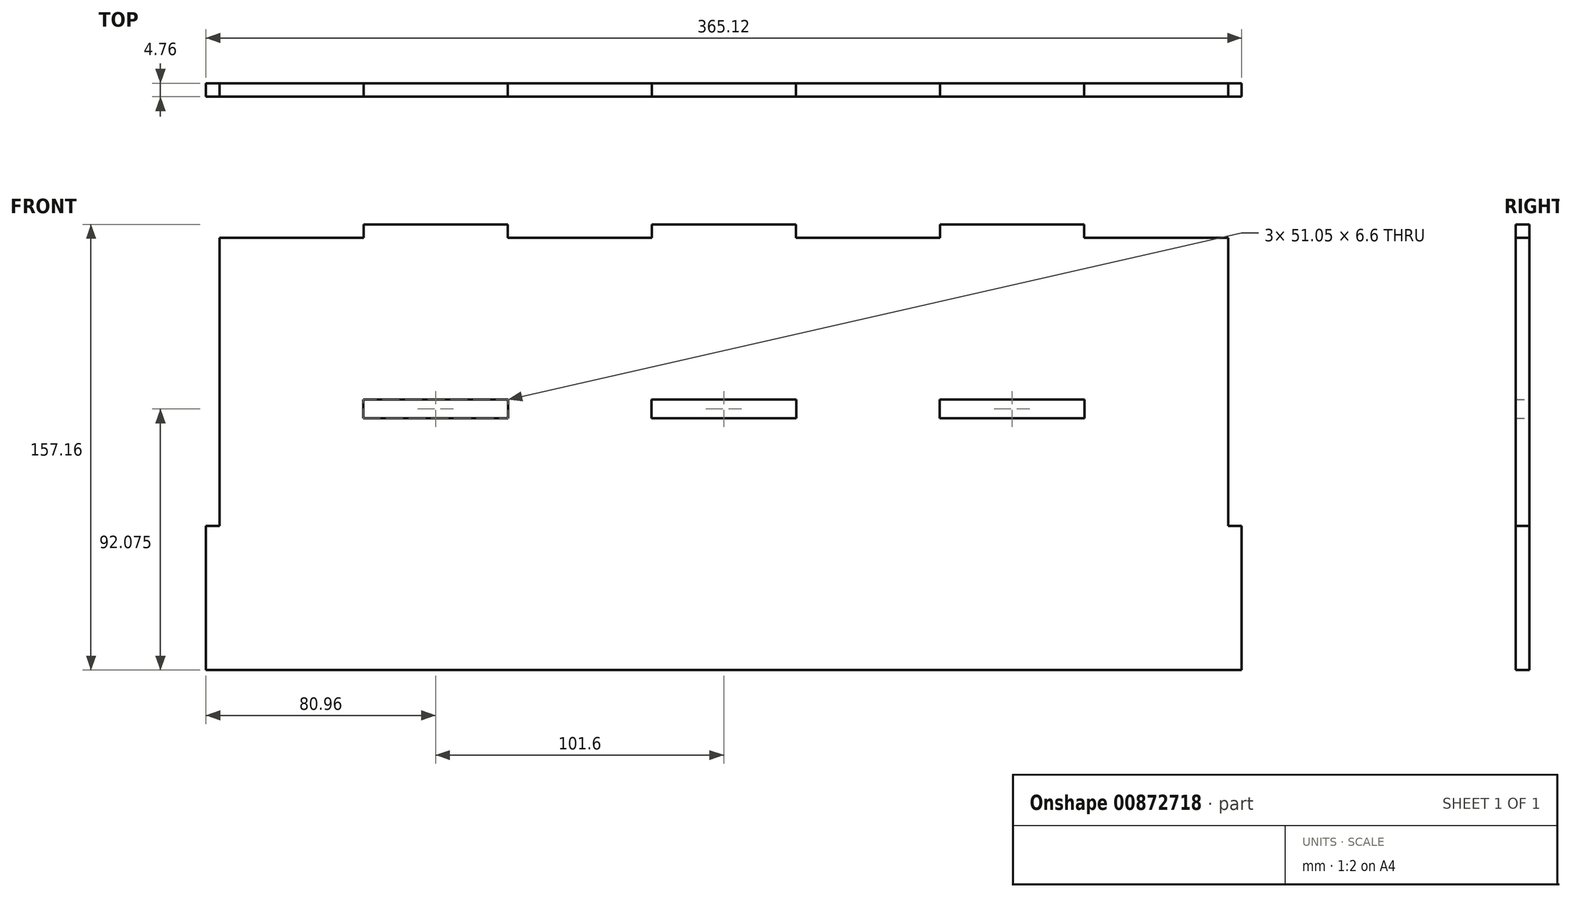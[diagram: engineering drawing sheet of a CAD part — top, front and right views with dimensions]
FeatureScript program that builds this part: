
annotation { "Feature Type Name" : "Feature", "Feature Type Description" : "" }
export const myFeature = defineFeature(function(context is Context, id is Id, definition is map)
    precondition{}
    {
        {
            var Q0;
            Q0=qCreatedBy(makeId("Front.planeOp"),FACE);
            var sketch = newSketch(context, id + "F0", { "sketchPlane" : qUnion([Q0])});
            skLineSegment(sketch, "E0.bottom", {"start": v(-182.56, 76.2) * mm, "end": v(182.56, 76.2) * mm});
            skLineSegment(sketch, "E0.top", {"start": v(-182.56, -76.2) * mm, "end": v(182.56, -76.2) * mm});
            skLineSegment(sketch, "E0.left", {"start": v(-182.56, 76.2) * mm, "end": v(-182.56, -76.2) * mm});
            skLineSegment(sketch, "E0.right", {"start": v(182.56, 76.2) * mm, "end": v(182.56, -76.2) * mm});
            skPoint(sketch, "E0.middle", {"position": v(0, 0) * mm});
            skLineSegment(sketch, "E1.0", {"start": v(-177.8, 76.2) * mm, "end": v(-177.8, -76.2) * mm});
            skLineSegment(sketch, "E2.0", {"start": v(177.8, 76.2) * mm, "end": v(177.8, -76.2) * mm});
            skLineSegment(sketch, "E3.bottom", {"start": v(-127, 19.05) * mm, "end": v(-76.2, 19.05) * mm});
            skLineSegment(sketch, "E3.top", {"start": v(-127, 12.7) * mm, "end": v(-76.2, 12.7) * mm});
            skLineSegment(sketch, "E3.left", {"start": v(-127, 19.05) * mm, "end": v(-127, 12.7) * mm});
            skLineSegment(sketch, "E3.right", {"start": v(-76.2, 19.05) * mm, "end": v(-76.2, 12.7) * mm});
            skLineSegment(sketch, "E4.0", {"start": v(-127.13, 19.18) * mm, "end": v(-76.07, 19.18) * mm});
            skLineSegment(sketch, "E4.1", {"start": v(-127.13, 19.18) * mm, "end": v(-127.13, 12.57) * mm});
            skLineSegment(sketch, "E4.2", {"start": v(-127.13, 12.57) * mm, "end": v(-76.07, 12.57) * mm});
            skLineSegment(sketch, "E4.3", {"start": v(-76.07, 19.18) * mm, "end": v(-76.07, 12.57) * mm});
            skLineSegment(sketch, "E5.1.0.0", {"start": v(-25.53, 19.18) * mm, "end": v(-25.53, 12.57) * mm});
            skLineSegment(sketch, "E5.1.0.1", {"start": v(-25.53, 19.18) * mm, "end": v(25.53, 19.18) * mm});
            skLineSegment(sketch, "E5.1.0.2", {"start": v(-25.53, 12.57) * mm, "end": v(25.53, 12.57) * mm});
            skLineSegment(sketch, "E5.1.0.3", {"start": v(25.4, 19.05) * mm, "end": v(25.4, 12.7) * mm});
            skLineSegment(sketch, "E5.1.0.4", {"start": v(-25.4, 19.05) * mm, "end": v(25.4, 19.05) * mm});
            skLineSegment(sketch, "E5.1.0.5", {"start": v(25.53, 19.18) * mm, "end": v(25.53, 12.57) * mm});
            skLineSegment(sketch, "E5.1.0.6", {"start": v(-25.4, 19.05) * mm, "end": v(-25.4, 12.7) * mm});
            skLineSegment(sketch, "E5.1.0.7", {"start": v(-25.4, 12.7) * mm, "end": v(25.4, 12.7) * mm});
            skLineSegment(sketch, "E5.2.0.0", {"start": v(76.07, 19.18) * mm, "end": v(76.07, 12.57) * mm});
            skLineSegment(sketch, "E5.2.0.1", {"start": v(76.07, 19.18) * mm, "end": v(127.13, 19.18) * mm});
            skLineSegment(sketch, "E5.2.0.2", {"start": v(76.07, 12.57) * mm, "end": v(127.13, 12.57) * mm});
            skLineSegment(sketch, "E5.2.0.3", {"start": v(127, 19.05) * mm, "end": v(127, 12.7) * mm});
            skLineSegment(sketch, "E5.2.0.4", {"start": v(76.2, 19.05) * mm, "end": v(127, 19.05) * mm});
            skLineSegment(sketch, "E5.2.0.5", {"start": v(127.13, 19.18) * mm, "end": v(127.13, 12.57) * mm});
            skLineSegment(sketch, "E5.2.0.6", {"start": v(76.2, 19.05) * mm, "end": v(76.2, 12.7) * mm});
            skLineSegment(sketch, "E5.2.0.7", {"start": v(76.2, 12.7) * mm, "end": v(127, 12.7) * mm});
            skLineSegment(sketch, "E5.direction1", {"start": v(-127, 12.7) * mm, "end": v(-25.4, 12.7) * mm, "construction": true});
            skLineSegment(sketch, "E6.bottom", {"start": v(-182.56, -76.2) * mm, "end": v(-177.8, -76.2) * mm});
            skLineSegment(sketch, "E6.top", {"start": v(-182.56, -25.4) * mm, "end": v(-177.8, -25.4) * mm});
            skLineSegment(sketch, "E6.left", {"start": v(-182.56, -76.2) * mm, "end": v(-182.56, -25.4) * mm});
            skLineSegment(sketch, "E6.right", {"start": v(-177.8, -76.2) * mm, "end": v(-177.8, -25.4) * mm});
            skLineSegment(sketch, "E7", {"start": v(0, 76.2) * mm, "end": v(0, -76.2) * mm, "construction": true});
            skLineSegment(sketch, "E8.MirrorCS", {"start": v(182.56, -76.2) * mm, "end": v(177.8, -76.2) * mm});
            skLineSegment(sketch, "E9.MirrorCS", {"start": v(182.56, -25.4) * mm, "end": v(177.8, -25.4) * mm});
            skLineSegment(sketch, "E10.MirrorCS", {"start": v(182.56, -76.2) * mm, "end": v(182.56, -25.4) * mm});
            skLineSegment(sketch, "E11.MirrorCS", {"start": v(177.8, -76.2) * mm, "end": v(177.8, -25.4) * mm});
            skLineSegment(sketch, "E12.bottom", {"start": v(-127, 76.2) * mm, "end": v(-76.2, 76.2) * mm});
            skLineSegment(sketch, "E12.top", {"start": v(-127, 80.96) * mm, "end": v(-76.2, 80.96) * mm});
            skLineSegment(sketch, "E12.left", {"start": v(-127, 76.2) * mm, "end": v(-127, 80.96) * mm});
            skLineSegment(sketch, "E12.right", {"start": v(-76.2, 76.2) * mm, "end": v(-76.2, 80.96) * mm});
            skLineSegment(sketch, "E13.1.0.0", {"start": v(-25.4, 76.2) * mm, "end": v(25.4, 76.2) * mm});
            skLineSegment(sketch, "E13.1.0.1", {"start": v(25.4, 76.2) * mm, "end": v(25.4, 80.96) * mm});
            skLineSegment(sketch, "E13.1.0.2", {"start": v(-25.4, 80.96) * mm, "end": v(25.4, 80.96) * mm});
            skLineSegment(sketch, "E13.1.0.3", {"start": v(-25.4, 76.2) * mm, "end": v(-25.4, 80.96) * mm});
            skLineSegment(sketch, "E13.2.0.0", {"start": v(76.2, 76.2) * mm, "end": v(127, 76.2) * mm});
            skLineSegment(sketch, "E13.2.0.1", {"start": v(127, 76.2) * mm, "end": v(127, 80.96) * mm});
            skLineSegment(sketch, "E13.2.0.2", {"start": v(76.2, 80.96) * mm, "end": v(127, 80.96) * mm});
            skLineSegment(sketch, "E13.2.0.3", {"start": v(76.2, 76.2) * mm, "end": v(76.2, 80.96) * mm});
            skLineSegment(sketch, "E13.direction1", {"start": v(-127, 76.2) * mm, "end": v(-25.4, 76.2) * mm, "construction": true});
            skSolve(sketch);
        }
        {
            var Q0;
            Q0=makeQuery(id+"F0.imprint","IMPRINT",FACE,{"disambiguationData":[TD([[makeQuery(id+"F0.imprint","IMPRINT",EDGE,{"derivedFrom":sQuery(id+"F0.wireOp",EDGE,"E4.0")}),1.0]])]});
            var Q1;
            {var subQ5=sQuery(id+"F0.wireOp",EDGE,"E9.MirrorCS");Q1=makeQuery(id+"F0.imprint","IMPRINT",FACE,{"disambiguationData":[TD([[makeQuery(id+"F0.imprint","IMPRINT",EDGE,{"derivedFrom":subQ5}),1.0]])]});}
            var Q2;
            {var subQ5=sQuery(id+"F0.wireOp",EDGE,"E6.top");Q2=makeQuery(id+"F0.imprint","IMPRINT",FACE,{"disambiguationData":[TD([[makeQuery(id+"F0.imprint","IMPRINT",EDGE,{"derivedFrom":subQ5}),-1.0]])]});}
            var Q3;
            Q3=makeQuery(id+"F0.imprint","IMPRINT",FACE,{"disambiguationData":[TD([[makeQuery(id+"F0.imprint","IMPRINT",EDGE,{"derivedFrom":sQuery(id+"F0.wireOp",EDGE,"E12.top")}),-1.0]])]});
            var Q4;
            {var subQ0=sQuery(id+"F0.wireOp",EDGE,"E13.1.0.1");Q4=makeQuery(id+"F0.imprint","IMPRINT",FACE,{"disambiguationData":[TD([[makeQuery(id+"F0.imprint","IMPRINT",EDGE,{"derivedFrom":subQ0}),1.0]])]});}
            var Q5;
            {var subQ2=sQuery(id+"F0.wireOp",EDGE,"E13.2.0.1");Q5=makeQuery(id+"F0.imprint","IMPRINT",FACE,{"disambiguationData":[TD([[makeQuery(id+"F0.imprint","IMPRINT",EDGE,{"derivedFrom":subQ2}),1.0]])]});}
            extrude(context, id + "F1", {"entities" : qUnion([Q0, Q1, Q2, Q3, Q4, Q5]), "depth" : 4.76 * mm, "offsetDistance" : 25.4 * mm});
        }
    });
